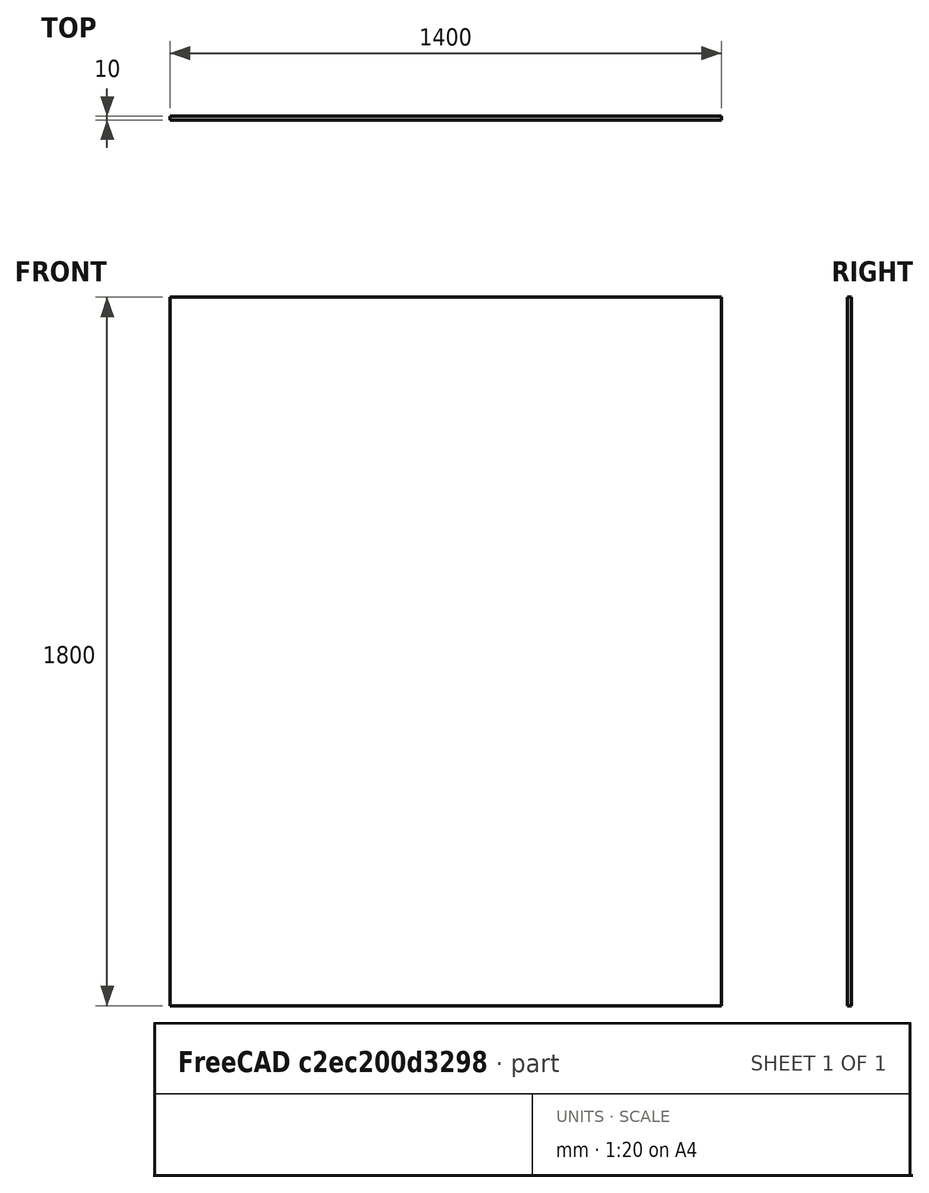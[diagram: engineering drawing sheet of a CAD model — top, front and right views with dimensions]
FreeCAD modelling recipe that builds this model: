
FCSTD DOCUMENT  (FreeCAD 1.0R39109 (Git))
Label: SlidingWardrobe
License: All rights reserved
LicenseURL: https://en.wikipedia.org/wiki/All_rights_reserved
objects: Sketcher::SketchObject×2, PartDesign::Pad×1, PartDesign::Body×1
note: 8 computed .brp shape members not serialized (recipe doc carries the construction recipe); baked Part::Feature solids carry a one-line shape summary decoded from their .brp

FEATURE [Sketcher::SketchObject] Sketch
  ArcFitTolerance = 1e-06
  AttachmentSupport = -> [XZ_Plane]
  FullyConstrained = true
  MakeInternals = false
  MapMode = 5
  Placement = pos=(0,0,0) rot=(1,0,0;1.5708rad)
  sketch-geometry (4):
    g0: LineSegment StartX=0 StartY=0 StartZ=0 EndX=1400 EndY=0 EndZ=0
    g1: LineSegment StartX=1400 StartY=0 StartZ=0 EndX=1400 EndY=1800 EndZ=0
    g2: LineSegment StartX=1400 StartY=1800 StartZ=0 EndX=0 EndY=1800 EndZ=0
    g3: LineSegment StartX=0 StartY=1800 StartZ=0 EndX=0 EndY=0 EndZ=0
  constraints (11):
    c: Coincident(g0,g1)
    c: Coincident(g1,g2)
    c: Coincident(g2,g3)
    c: Coincident(g3,g0)
    c: Horizontal(g0)
    c: Horizontal(g2)
    c: Vertical(g1)
    c: Vertical(g3)
    c: Coincident(g0,g-1)
    c: DistanceX(g2,g2) = 1400  'door_internal_length'
    c: DistanceY(g3,g3) = 1800  'door_internal_height'
FEATURE [PartDesign::Pad] Pad
  Direction = (0,-1,2e-16)
  Length = 10
  Length2 = 10
  Placement = pos=(0,0,0) rot=(1,0,0;1.5708rad)
  Profile = -> Sketch
  ReferenceAxis = -> Sketch [N_Axis]
  Refine = true
  Suppressed = false
  Type = 0
FEATURE [Sketcher::SketchObject] Sketch001
  ArcFitTolerance = 1e-06
  AttachmentSupport = -> [Pad]
  ExternalGeometry = -> [Pad]
  FullyConstrained = false
  MakeInternals = false
  MapMode = 5
  Placement = pos=(0,3.997e-13,1800) rot=(0,0,1;3.14159rad)
  sketch-geometry (8):
    g0: LineSegment StartX=0 StartY=10 StartZ=0 EndX=0 EndY=0 EndZ=0
    g1: LineSegment StartX=0 StartY=0 StartZ=0 EndX=-6.65331 EndY=0 EndZ=0
    g2: LineSegment StartX=-6.65331 StartY=0 StartZ=0 EndX=-6.65331 EndY=-0.956299 EndZ=0
    g3: LineSegment StartX=-6.65331 StartY=-0.956299 StartZ=0 EndX=10.8186 EndY=-0.956299 EndZ=0
    g4: LineSegment StartX=0 StartY=10 StartZ=0 EndX=-8.0066 EndY=10 EndZ=0
    g5: LineSegment StartX=-8.0066 StartY=10 StartZ=0 EndX=-8.0066 EndY=11.4428 EndZ=0
    g6: LineSegment StartX=-8.0066 StartY=11.4428 StartZ=0 EndX=2.01877 EndY=11.4428 EndZ=0
    g7: ArcOfCircle CenterX=4.14139 CenterY=11.1573 CenterZ=0 NormalX=0 NormalY=0 NormalZ=1 AngleXU=0 Radius=13.832 StartAngle=5.21617 EndAngle=6.55935
  constraints (15):
    c: Coincident(g-3,g0)
    c: Coincident(g0,g-1)
    c: Coincident(g0,g1)
    c: PointOnObject(g1,g-1)
    c: Coincident(g1,g2)
    c: Vertical(g2)
    c: Coincident(g2,g3)
    c: Horizontal(g3)
    c: Coincident(g0,g4)
    c: Horizontal(g4)
    c: Coincident(g4,g5)
    c: Vertical(g5)
    c: Coincident(g5,g6)
    c: Horizontal(g6)
    c: Coincident(g7,g3)
FEATURE [PartDesign::Body] Body
  AllowCompound = false
  Group = -> [Sketch,Pad,Sketch001]
  Origin = -> Origin
  Tip = -> Pad
